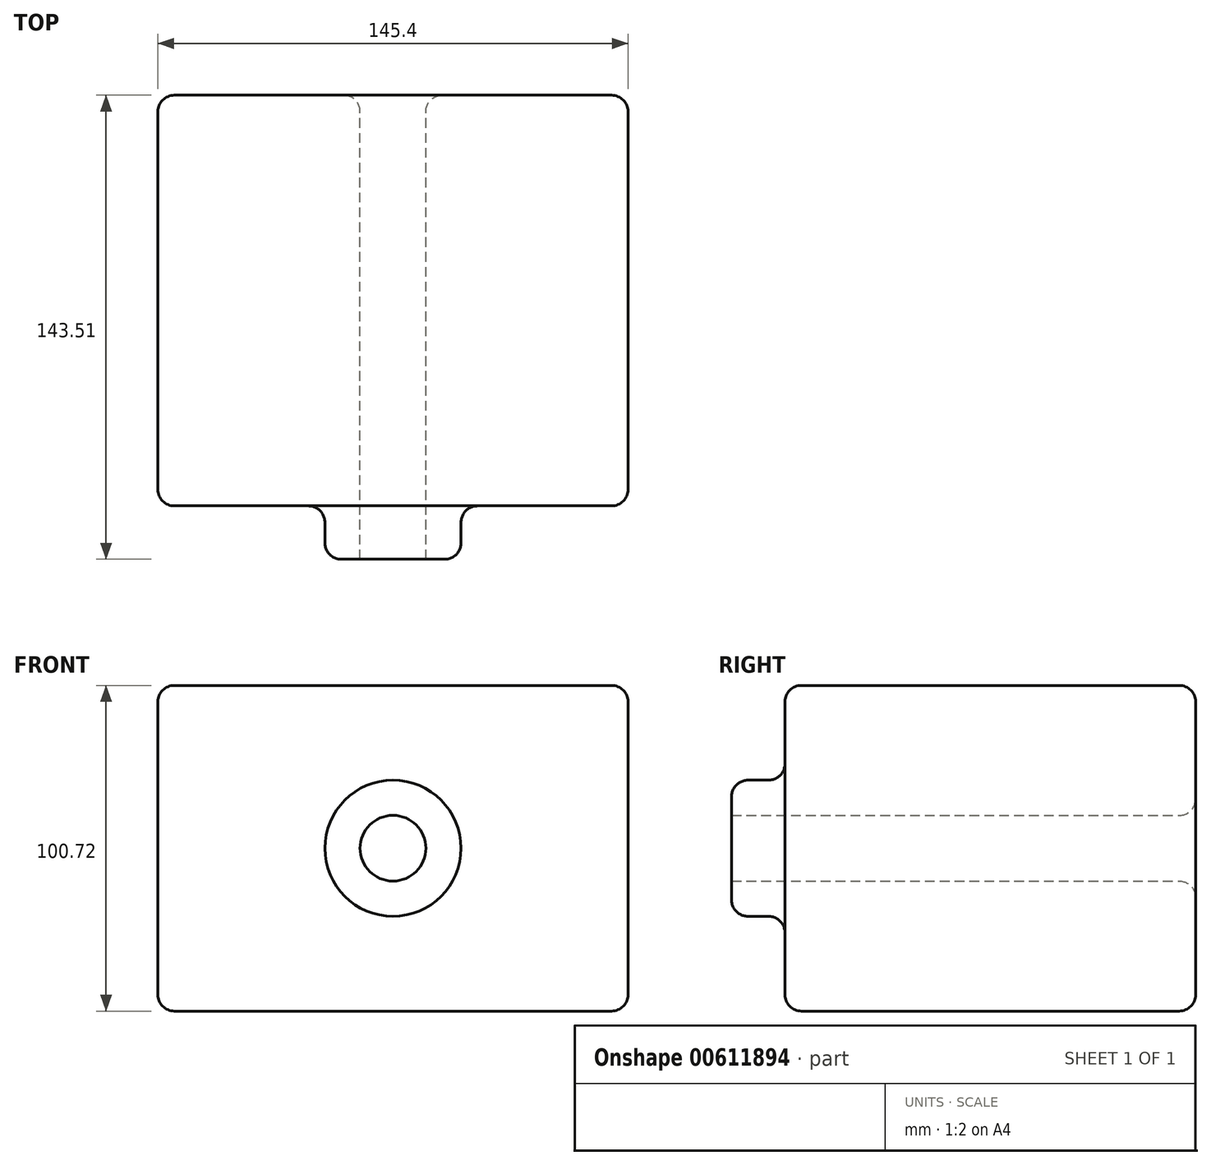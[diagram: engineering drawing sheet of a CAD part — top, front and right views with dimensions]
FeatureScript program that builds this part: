
annotation { "Feature Type Name" : "Feature", "Feature Type Description" : "" }
export const myFeature = defineFeature(function(context is Context, id is Id, definition is map)
    precondition{}
    {
        {
            var Q0;
            Q0=qCreatedBy(makeId("Front.planeOp"),FACE);
            var sketch = newSketch(context, id + "F0", { "sketchPlane" : qUnion([Q0])});
            skLineSegment(sketch, "E0.bottom", {"start": v(-72.7, 50.36) * mm, "end": v(72.7, 50.36) * mm});
            skLineSegment(sketch, "E0.top", {"start": v(-72.7, -50.36) * mm, "end": v(72.7, -50.36) * mm});
            skLineSegment(sketch, "E0.left", {"start": v(-72.7, 50.36) * mm, "end": v(-72.7, -50.36) * mm});
            skLineSegment(sketch, "E0.right", {"start": v(72.7, 50.36) * mm, "end": v(72.7, -50.36) * mm});
            skPoint(sketch, "E0.middle", {"position": v(0, 0) * mm});
            skSolve(sketch);
        }
        {
            var Q0;
            Q0=makeQuery(id+"F0.imprint","IMPRINT",FACE,{"disambiguationData":[TD([[makeQuery(id+"F0.imprint","IMPRINT",EDGE,{"derivedFrom":sQuery(id+"F0.wireOp",EDGE,"E0.bottom")}),-1.0]])]});
            var sketch = newSketch(context, id + "F1", { "sketchPlane" : qUnion([Q0])});
            skCircle(sketch, "E1", {"center": v(0, 0) * mm, "radius": 21.05 * mm});
            skCircle(sketch, "E2", {"center": v(0, 0) * mm, "radius": 10.16 * mm});
            skSolve(sketch);
        }
        {
            var Q0;
            Q0=makeQuery(id+"F0.imprint","IMPRINT",FACE,{"disambiguationData":[TD([[makeQuery(id+"F0.imprint","IMPRINT",EDGE,{"derivedFrom":sQuery(id+"F0.wireOp",EDGE,"E0.bottom")}),-1.0]])]});
            extrude(context, id + "F2", {"entities" : qUnion([Q0]), "endBound" : BoundingType.SYMMETRIC, "depth" : 127 * mm, "offsetDistance" : 25.4 * mm});
        }
        {
            var Q0;
            Q0 = qSketchRegion(id + "F1", true);
            extrude(context, id + "F3", {"entities" : qUnion([Q0]), "operationType" : NewBodyOperationType.ADD, "depth" : 80 * mm, "offsetDistance" : 25.4 * mm});
        }
        {
            var Q0;
            Q0=makeQuery(id+"F3.boolean.opBoolean","SPLIT",FACE,{"disambiguationData":[TD([makeQuery(id+"F3.opExtrude","SWEPT_FACE",FACE,{"disambiguationData":[OSD([sQuery(id+"F1.wireOp",EDGE,"E2")])]})])],"derivedFrom":makeQuery(id+"F2.opExtrude","CAP_FACE",FACE,{"disambiguationData":[OSD([sQuery(id+"F0.wireOp",EDGE,"E0.bottom"),sQuery(id+"F0.wireOp",EDGE,"E0.top"),sQuery(id+"F0.wireOp",EDGE,"E0.left"),sQuery(id+"F0.wireOp",EDGE,"E0.right")])],"isStart":false})});
            extrude(context, id + "F4", {"entities" : qUnion([Q0]), "operationType" : NewBodyOperationType.REMOVE, "oppositeDirection" : true, "depth" : 127 * mm, "offsetDistance" : 25.4 * mm});
        }
        {
            var Q0;
            Q0=makeQuery(id+"F2.opExtrude","CAP_EDGE",EDGE,{"disambiguationData":[OSD([sQuery(id+"F0.wireOp",EDGE,"E0.bottom")])],"isStart":false});
            var Q1;
            Q1=makeQuery(id+"F2.opExtrude","CAP_EDGE",EDGE,{"disambiguationData":[OSD([sQuery(id+"F0.wireOp",EDGE,"E0.left")])],"isStart":false});
            var Q2;
            Q2=makeQuery(id+"F2.opExtrude","CAP_EDGE",EDGE,{"disambiguationData":[OSD([sQuery(id+"F0.wireOp",EDGE,"E0.top")])],"isStart":false});
            var Q3;
            {var subQ0=sQuery(id+"F0.wireOp",EDGE,"E0.left");var subQ1=sQuery(id+"F0.wireOp",EDGE,"E0.top");var subQ2=sQuery(id+"F0.wireOp",EDGE,"E0.right");var subQ3=sQuery(id+"F0.wireOp",EDGE,"E0.bottom");Q3=makeQuery(id+"F3.boolean.opBoolean","SPLIT",FACE,{"disambiguationData":[TD([makeQuery(id+"F2.opExtrude","SWEPT_FACE",FACE,{"disambiguationData":[OSD([subQ3])]})])],"derivedFrom":makeQuery(id+"F2.opExtrude","CAP_FACE",FACE,{"disambiguationData":[OSD([subQ3,subQ1,subQ0,subQ2])],"isStart":false})});}
            var Q4;
            Q4=makeQuery(id+"F2.opExtrude","CAP_EDGE",EDGE,{"disambiguationData":[OSD([sQuery(id+"F0.wireOp",EDGE,"E0.bottom")])],"isStart":true});
            var Q5;
            Q5=makeQuery(id+"F2.opExtrude","SWEPT_FACE",FACE,{"disambiguationData":[OSD([sQuery(id+"F0.wireOp",EDGE,"E0.bottom")])]});
            var Q6;
            Q6=makeQuery(id+"F2.opExtrude","CAP_EDGE",EDGE,{"disambiguationData":[OSD([sQuery(id+"F0.wireOp",EDGE,"E0.left")])],"isStart":true});
            var Q7;
            Q7=makeQuery(id+"F2.opExtrude","SWEPT_FACE",FACE,{"disambiguationData":[OSD([sQuery(id+"F0.wireOp",EDGE,"E0.left")])]});
            var Q8;
            Q8=makeQuery(id+"F2.opExtrude","CAP_EDGE",EDGE,{"disambiguationData":[OSD([sQuery(id+"F0.wireOp",EDGE,"E0.right")])],"isStart":true});
            var Q9;
            Q9=makeQuery(id+"F2.opExtrude","SWEPT_EDGE",EDGE,{"disambiguationData":[OSD([sQuery(id+"F0.wireOp",EDGE,"E0.top"),sQuery(id+"F0.wireOp",EDGE,"E0.right")])]});
            var Q10;
            Q10=makeQuery(id+"F3.opExtrude","CAP_EDGE",EDGE,{"disambiguationData":[OSD([sQuery(id+"F1.wireOp",EDGE,"E1")])],"isStart":false});
            var Q11;
            Q11=makeQuery(id+"F2.opExtrude","CAP_FACE",FACE,{"disambiguationData":[OSD([sQuery(id+"F0.wireOp",EDGE,"E0.bottom"),sQuery(id+"F0.wireOp",EDGE,"E0.top"),sQuery(id+"F0.wireOp",EDGE,"E0.left"),sQuery(id+"F0.wireOp",EDGE,"E0.right")])],"isStart":true});
            fillet(context, id + "F5", {"entities" : qUnion([Q0, Q1, Q2, Q3, Q4, Q5, Q6, Q7, Q8, Q9, Q10, Q11]), "radius" : 5.08 * mm, "tangentPropagation" : true, "allowEdgeOverflow" : false});
        }
    });
